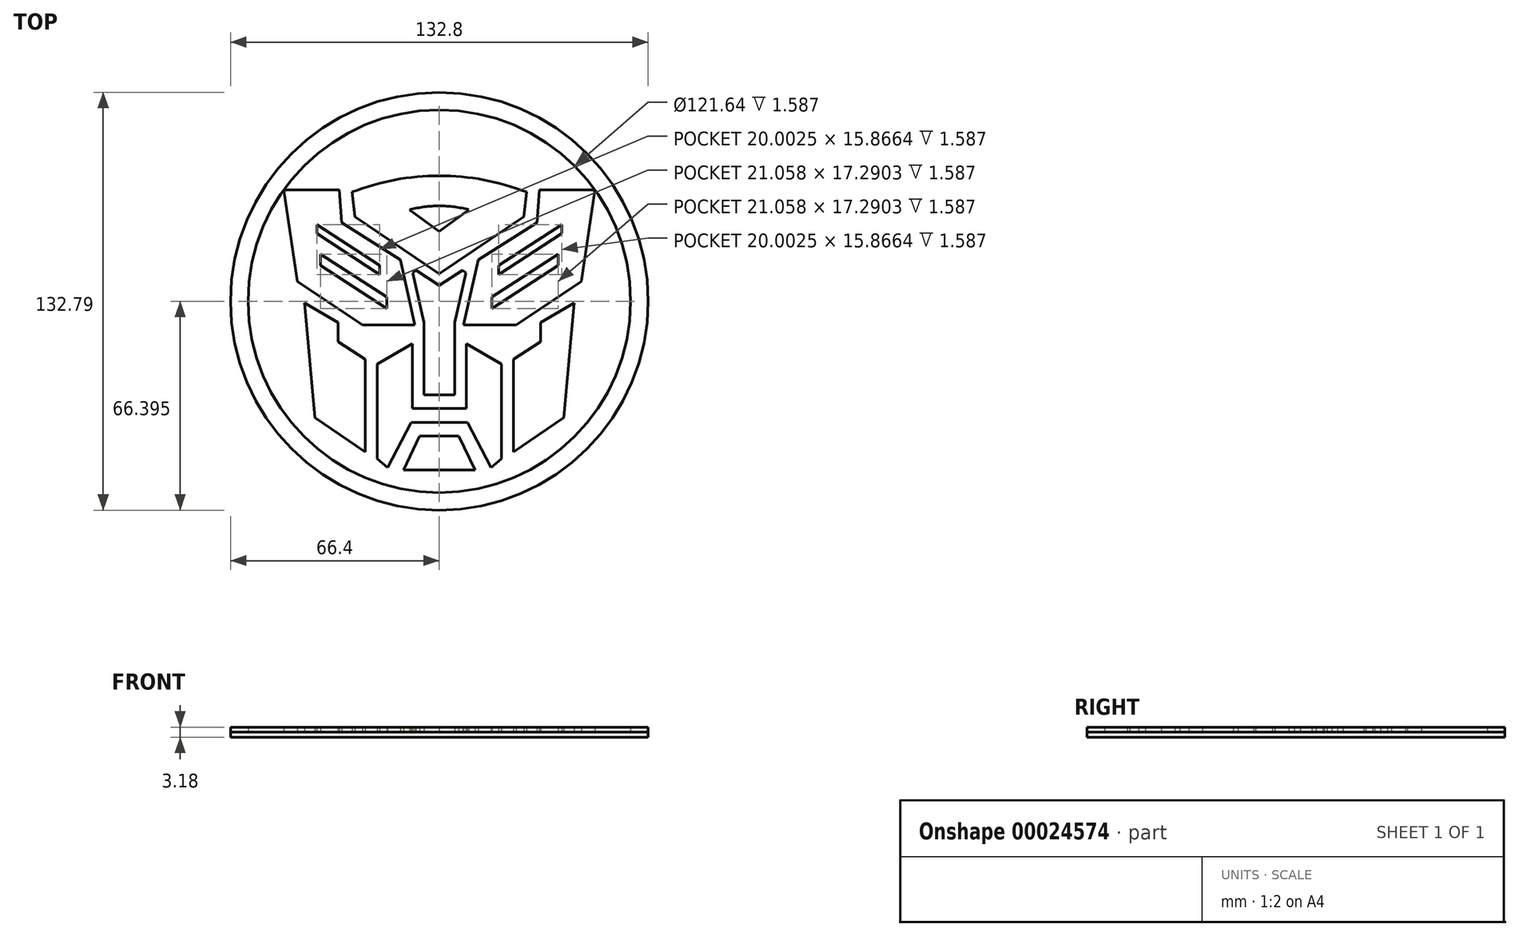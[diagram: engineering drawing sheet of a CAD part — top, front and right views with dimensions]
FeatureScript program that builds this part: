
annotation { "Feature Type Name" : "Feature", "Feature Type Description" : "" }
export const myFeature = defineFeature(function(context is Context, id is Id, definition is map)
    precondition{}
    {
        {
            var Q0;
            Q0=qCreatedBy(makeId("Top.planeOp"),FACE);
            var sketch = newSketch(context, id + "F0", { "sketchPlane" : qUnion([Q0])});
            skLineSegment(sketch, "E0", {"start": v(-54.27, 0) * mm, "end": v(54.27, 0) * mm, "construction": true});
            skLineSegment(sketch, "E1", {"start": v(0, 0) * mm, "end": v(0, 50.8) * mm, "construction": true});
            skCircle(sketch, "E2", {"center": v(0, 6.81) * mm, "radius": 66.4 * mm});
            skSolve(sketch);
        }
        {
            var Q0;
            Q0 = qSketchRegion(id + "F0", true);
            extrude(context, id + "F1", {"entities" : qUnion([Q0]), "depth" : 1.59 * mm});
        }
        {
            var Q0;
            Q0=makeQuery(id+"F1.opExtrude","CAP_FACE",FACE,{"disambiguationData":[OSD([sQuery(id+"F0.wireOp",EDGE,"E2")])],"isStart":false});
            var sketch = newSketch(context, id + "F2", { "sketchPlane" : qUnion([Q0])});
            skLineSegment(sketch, "E3", {"start": v(0, 0) * mm, "end": v(0, 61.3) * mm, "construction": true});
            skLineSegment(sketch, "E4", {"start": v(-49.43, 42.26) * mm, "end": v(-31.85, 42.26) * mm});
            skLineSegment(sketch, "E5", {"start": v(-31.85, 42.26) * mm, "end": v(-31.07, 31.82) * mm});
            skLineSegment(sketch, "E6", {"start": v(-31.07, 31.82) * mm, "end": v(-12.42, 19.95) * mm});
            skLineSegment(sketch, "E7", {"start": v(-12.42, 19.95) * mm, "end": v(-7.75, -0.73) * mm});
            skLineSegment(sketch, "E8", {"start": v(-7.75, -0.73) * mm, "end": v(-24.43, -0.73) * mm});
            skLineSegment(sketch, "E9", {"start": v(-24.43, -0.73) * mm, "end": v(-45.17, 13.1) * mm});
            skLineSegment(sketch, "E10", {"start": v(-45.17, 13.1) * mm, "end": v(-49.43, 42.26) * mm});
            skLineSegment(sketch, "E11", {"start": v(-38.94, 31.2) * mm, "end": v(-18.93, 18.19) * mm});
            skLineSegment(sketch, "E12", {"start": v(-18.93, 18.19) * mm, "end": v(-18.93, 15.34) * mm});
            skLineSegment(sketch, "E13", {"start": v(-18.93, 15.34) * mm, "end": v(-38.94, 28.36) * mm});
            skLineSegment(sketch, "E14", {"start": v(-38.94, 28.36) * mm, "end": v(-38.94, 31.2) * mm});
            skLineSegment(sketch, "E15", {"start": v(-37.75, 21.83) * mm, "end": v(-16.69, 8.12) * mm});
            skLineSegment(sketch, "E16", {"start": v(-16.69, 8.12) * mm, "end": v(-16.69, 4.54) * mm});
            skLineSegment(sketch, "E17", {"start": v(-16.69, 4.54) * mm, "end": v(-37.75, 18.24) * mm});
            skLineSegment(sketch, "E18", {"start": v(-37.75, 18.24) * mm, "end": v(-37.75, 21.83) * mm});
            skLineSegment(sketch, "E19", {"start": v(0, 11.9) * mm, "end": v(-7.4, 16.7) * mm});
            skLineSegment(sketch, "E20", {"start": v(-7.4, 16.7) * mm, "end": v(-8.5, 15.8) * mm});
            skLineSegment(sketch, "E21", {"start": v(-8.5, 15.8) * mm, "end": v(-4.85, 0) * mm});
            skLineSegment(sketch, "E22", {"start": v(-4.85, 0) * mm, "end": v(-4.85, -22.99) * mm});
            skLineSegment(sketch, "E23", {"start": v(-4.85, -22.99) * mm, "end": v(0, -22.99) * mm});
            skLineSegment(sketch, "E24", {"start": v(-42.9, 6.24) * mm, "end": v(-32.16, 0) * mm});
            skLineSegment(sketch, "E25", {"start": v(-32.16, 0) * mm, "end": v(-32.16, -6.1) * mm});
            skLineSegment(sketch, "E26", {"start": v(-32.16, -6.1) * mm, "end": v(-23.62, -11.58) * mm});
            skLineSegment(sketch, "E27", {"start": v(-23.62, -11.58) * mm, "end": v(-23.62, -41.1) * mm});
            skLineSegment(sketch, "E28", {"start": v(-23.62, -41.1) * mm, "end": v(-39.58, -30.2) * mm});
            skLineSegment(sketch, "E29", {"start": v(-39.58, -30.2) * mm, "end": v(-42.9, 6.24) * mm});
            skLineSegment(sketch, "E30", {"start": v(0, -27.22) * mm, "end": v(-8.54, -27.22) * mm});
            skLineSegment(sketch, "E31", {"start": v(-8.54, -27.22) * mm, "end": v(-8.54, -6.66) * mm});
            skLineSegment(sketch, "E32", {"start": v(-8.54, -6.66) * mm, "end": v(-19.75, -13.11) * mm});
            skLineSegment(sketch, "E33", {"start": v(-19.75, -13.11) * mm, "end": v(-19.75, -43.27) * mm});
            skLineSegment(sketch, "E34", {"start": v(-19.75, -43.27) * mm, "end": v(-16.44, -46.1) * mm});
            skLineSegment(sketch, "E35", {"start": v(-16.44, -46.1) * mm, "end": v(-8.94, -31.66) * mm});
            skLineSegment(sketch, "E36", {"start": v(-8.94, -31.66) * mm, "end": v(0, -31.66) * mm});
            skLineSegment(sketch, "E37", {"start": v(0, -46.83) * mm, "end": v(-11.35, -46.83) * mm});
            skLineSegment(sketch, "E38", {"start": v(-11.35, -46.83) * mm, "end": v(-6.21, -36) * mm});
            skLineSegment(sketch, "E39", {"start": v(-6.21, -36) * mm, "end": v(0, -36) * mm});
            skLineSegment(sketch, "E40", {"start": v(0, 15.58) * mm, "end": v(-26.92, 33.7) * mm});
            skLineSegment(sketch, "E41", {"start": v(-26.92, 33.7) * mm, "end": v(-27.72, 41.52) * mm});
            skArc(sketch, "E42", {"start": v(0, 46.72) * mm, "mid": v(-14.1, 45.4) * mm, "end": v(-27.72, 41.52) * mm});
            skLineSegment(sketch, "E43", {"start": v(0, 29) * mm, "end": v(-9.4, 35.9) * mm});
            skArc(sketch, "E44", {"start": v(0, 37.15) * mm, "mid": v(-4.74, 36.84) * mm, "end": v(-9.4, 35.9) * mm});
            skLineSegment(sketch, "E45.MirrorCS", {"start": v(16.69, 8.12) * mm, "end": v(16.69, 4.54) * mm});
            skLineSegment(sketch, "E46.MirrorCS", {"start": v(7.4, 16.7) * mm, "end": v(8.5, 15.8) * mm});
            skLineSegment(sketch, "E47.MirrorCS", {"start": v(37.75, 18.24) * mm, "end": v(37.75, 21.83) * mm});
            skLineSegment(sketch, "E48.MirrorCS", {"start": v(38.94, 28.36) * mm, "end": v(38.94, 31.2) * mm});
            skLineSegment(sketch, "E49.MirrorCS", {"start": v(32.16, 0) * mm, "end": v(32.16, -6.1) * mm});
            skLineSegment(sketch, "E50.MirrorCS", {"start": v(18.93, 18.19) * mm, "end": v(18.93, 15.34) * mm});
            skLineSegment(sketch, "E51.MirrorCS", {"start": v(19.75, -43.27) * mm, "end": v(16.44, -46.1) * mm});
            skLineSegment(sketch, "E52.MirrorCS", {"start": v(4.85, -22.99) * mm, "end": v(0, -22.99) * mm});
            skLineSegment(sketch, "E53.MirrorCS", {"start": v(0, -27.22) * mm, "end": v(8.54, -27.22) * mm});
            skArc(sketch, "E54.MirrorCS", {"start": v(0, 46.72) * mm, "mid": v(14.1, 45.4) * mm, "end": v(27.72, 41.52) * mm});
            skLineSegment(sketch, "E55.MirrorCS", {"start": v(8.54, -6.66) * mm, "end": v(19.75, -13.11) * mm});
            skLineSegment(sketch, "E56.MirrorCS", {"start": v(6.21, -36) * mm, "end": v(0, -36) * mm});
            skLineSegment(sketch, "E57.MirrorCS", {"start": v(16.69, 4.54) * mm, "end": v(37.75, 18.24) * mm});
            skLineSegment(sketch, "E58.MirrorCS", {"start": v(4.85, 0) * mm, "end": v(4.85, -22.99) * mm});
            skLineSegment(sketch, "E59.MirrorCS", {"start": v(8.94, -31.66) * mm, "end": v(0, -31.66) * mm});
            skLineSegment(sketch, "E60.MirrorCS", {"start": v(49.43, 42.26) * mm, "end": v(31.85, 42.26) * mm});
            skLineSegment(sketch, "E61.MirrorCS", {"start": v(31.85, 42.26) * mm, "end": v(31.07, 31.82) * mm});
            skLineSegment(sketch, "E62.MirrorCS", {"start": v(42.9, 6.24) * mm, "end": v(32.16, 0) * mm});
            skLineSegment(sketch, "E63.MirrorCS", {"start": v(19.75, -13.11) * mm, "end": v(19.75, -43.27) * mm});
            skLineSegment(sketch, "E64.MirrorCS", {"start": v(12.42, 19.95) * mm, "end": v(7.75, -0.73) * mm});
            skLineSegment(sketch, "E65.MirrorCS", {"start": v(31.07, 31.82) * mm, "end": v(12.42, 19.95) * mm});
            skLineSegment(sketch, "E66.MirrorCS", {"start": v(0, 15.58) * mm, "end": v(26.92, 33.7) * mm});
            skLineSegment(sketch, "E67.MirrorCS", {"start": v(0, 11.9) * mm, "end": v(7.4, 16.7) * mm});
            skLineSegment(sketch, "E68.MirrorCS", {"start": v(11.35, -46.83) * mm, "end": v(6.21, -36) * mm});
            skLineSegment(sketch, "E69.MirrorCS", {"start": v(16.44, -46.1) * mm, "end": v(8.94, -31.66) * mm});
            skLineSegment(sketch, "E70.MirrorCS", {"start": v(0, 29) * mm, "end": v(9.4, 35.9) * mm});
            skLineSegment(sketch, "E71.MirrorCS", {"start": v(7.75, -0.73) * mm, "end": v(24.43, -0.73) * mm});
            skLineSegment(sketch, "E72.MirrorCS", {"start": v(24.43, -0.73) * mm, "end": v(45.17, 13.1) * mm});
            skLineSegment(sketch, "E73.MirrorCS", {"start": v(8.54, -27.22) * mm, "end": v(8.54, -6.66) * mm});
            skLineSegment(sketch, "E74.MirrorCS", {"start": v(37.75, 21.83) * mm, "end": v(16.69, 8.12) * mm});
            skLineSegment(sketch, "E75.MirrorCS", {"start": v(0, -46.83) * mm, "end": v(11.35, -46.83) * mm});
            skLineSegment(sketch, "E76.MirrorCS", {"start": v(26.92, 33.7) * mm, "end": v(27.72, 41.52) * mm});
            skLineSegment(sketch, "E77.MirrorCS", {"start": v(38.94, 31.2) * mm, "end": v(18.93, 18.19) * mm});
            skLineSegment(sketch, "E78.MirrorCS", {"start": v(18.93, 15.34) * mm, "end": v(38.94, 28.36) * mm});
            skLineSegment(sketch, "E79.MirrorCS", {"start": v(8.5, 15.8) * mm, "end": v(4.85, 0) * mm});
            skArc(sketch, "E80.MirrorCS", {"start": v(0, 37.15) * mm, "mid": v(4.74, 36.84) * mm, "end": v(9.4, 35.9) * mm});
            skLineSegment(sketch, "E81.MirrorCS", {"start": v(45.17, 13.1) * mm, "end": v(49.43, 42.26) * mm});
            skLineSegment(sketch, "E82.MirrorCS", {"start": v(32.16, -6.1) * mm, "end": v(23.62, -11.58) * mm});
            skLineSegment(sketch, "E83.MirrorCS", {"start": v(23.62, -11.58) * mm, "end": v(23.62, -41.1) * mm});
            skLineSegment(sketch, "E84.MirrorCS", {"start": v(23.62, -41.1) * mm, "end": v(39.58, -30.2) * mm});
            skLineSegment(sketch, "E85.MirrorCS", {"start": v(39.58, -30.2) * mm, "end": v(42.9, 6.24) * mm});
            skSolve(sketch);
        }
        {
            var Q0;
            Q0 = qSketchRegion(id + "F2", true);
            extrude(context, id + "F3", {"entities" : qUnion([Q0]), "operationType" : NewBodyOperationType.ADD, "depth" : 1.59 * mm});
        }
        {
            var Q0;
            {var subQ0=sQuery(id+"F0.wireOp",EDGE,"E2");Q0=makeQuery(id+"F3.boolean.opBoolean","SPLIT",FACE,{"disambiguationData":[TD([makeQuery(id+"F1.opExtrude","SWEPT_FACE",FACE,{"disambiguationData":[OSD([subQ0])]})])],"derivedFrom":makeQuery(id+"F1.opExtrude","CAP_FACE",FACE,{"disambiguationData":[OSD([subQ0])],"isStart":false})});}
            var sketch = newSketch(context, id + "F4", { "sketchPlane" : qUnion([Q0])});
            skCircle(sketch, "E86.0", {"center": v(0, 6.81) * mm, "radius": 66.4 * mm});
            skCircle(sketch, "E87", {"center": v(0, 6.81) * mm, "radius": 60.82 * mm});
            skSolve(sketch);
        }
        {
            var Q0;
            Q0 = qSketchRegion(id + "F4", true);
            extrude(context, id + "F5", {"entities" : qUnion([Q0]), "depth" : 1.59 * mm});
        }
    });
